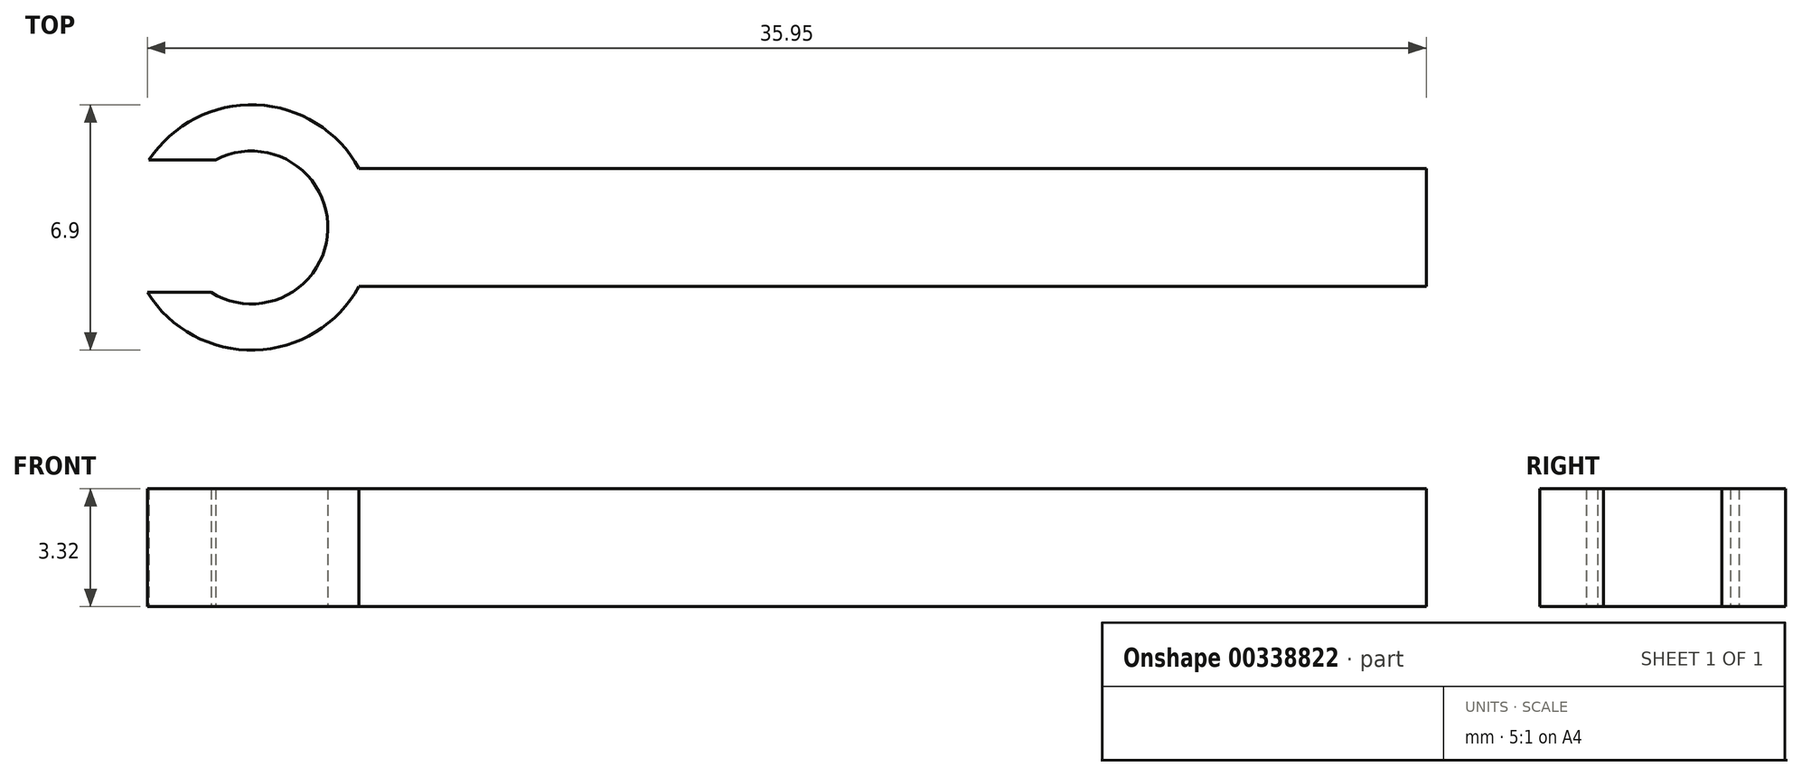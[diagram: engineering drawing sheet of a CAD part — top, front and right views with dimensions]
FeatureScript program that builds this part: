
annotation { "Feature Type Name" : "Feature", "Feature Type Description" : "" }
export const myFeature = defineFeature(function(context is Context, id is Id, definition is map)
    precondition{}
    {
        {
            var Q0;
            Q0=qCreatedBy(makeId("Top.planeOp"),FACE);
            var sketch = newSketch(context, id + "F0", { "sketchPlane" : qUnion([Q0])});
            skArc(sketch, "E0", {"start": v(-5.85, 0) * mm, "mid": v(0.52, 1.78) * mm, "end": v(-5.8, 3.73) * mm});
            skPoint(sketch, "E0.third.point", {"position": v(-6.38, 1.83) * mm});
            skPoint(sketch, "E0.third.point.positionSnap0", {"position": v(0, 1.83) * mm});
            skPoint(sketch, "E1", {"position": v(-5.8, 3.73) * mm});
            skPoint(sketch, "E2", {"position": v(-5.85, 0) * mm});
            skArc(sketch, "E3", {"start": v(-4.06, 0) * mm, "mid": v(-0.78, 1.75) * mm, "end": v(-3.93, 3.73) * mm});
            skLineSegment(sketch, "E4", {"start": v(-5.8, 3.73) * mm, "end": v(-3.93, 3.73) * mm});
            skLineSegment(sketch, "E5", {"start": v(-5.85, 0) * mm, "end": v(-4.06, 0) * mm});
            skPoint(sketch, "E6.top.start.orphan", {"position": v(0, 3.65) * mm});
            skPoint(sketch, "E6.left.start.orphan", {"position": v(0, 0) * mm});
            skLineSegment(sketch, "E7", {"start": v(0.1, 3.49) * mm, "end": v(0.1, 0.17) * mm});
            skLineSegment(sketch, "E8", {"start": v(0.1, 0.17) * mm, "end": v(30.1, 0.17) * mm});
            skLineSegment(sketch, "E9.top", {"start": v(0.1, 3.49) * mm, "end": v(30.1, 3.49) * mm});
            skLineSegment(sketch, "E9.left", {"start": v(0.1, 0.17) * mm, "end": v(0.1, 3.49) * mm});
            skLineSegment(sketch, "E9.right", {"start": v(30.1, 0.17) * mm, "end": v(30.1, 3.49) * mm});
            skSolve(sketch);
        }
        {
            var Q0;
            Q0 = qSketchRegion(id + "F0", true);
            extrude(context, id + "F1", {"entities" : qUnion([Q0]), "depth" : 3.32 * mm});
        }
    });
